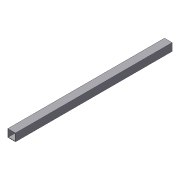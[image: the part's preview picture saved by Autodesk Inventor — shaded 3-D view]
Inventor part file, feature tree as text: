
AUTODESK INVENTOR PART (.ipt)
format: ipt  version: 2012 (Build 160160000, 160)  size: 71,680 bytes
history: native  units: in
note: dims shown in document units (in); Inventor stores cm internally (conversion verified against a paired STEP export)
features: extrude x1, shell x1, sketch x1
ambient origin geometry x8: Origin, YZ Plane, XZ Plane, XY Plane, X Axis, Y Axis, Z Axis, Center Point
bodies: Solid1 (feature_tree)
feature tree (3):
  extrude  "Extrusion1"  Depth=1.0in
  shell  "Shell1"  Thickness=20.5in
  sketch  "Sketch1"  dims[d0=1.0in d1=1.0in d2=20.5in d3=0.0in d4=0.0625in]
